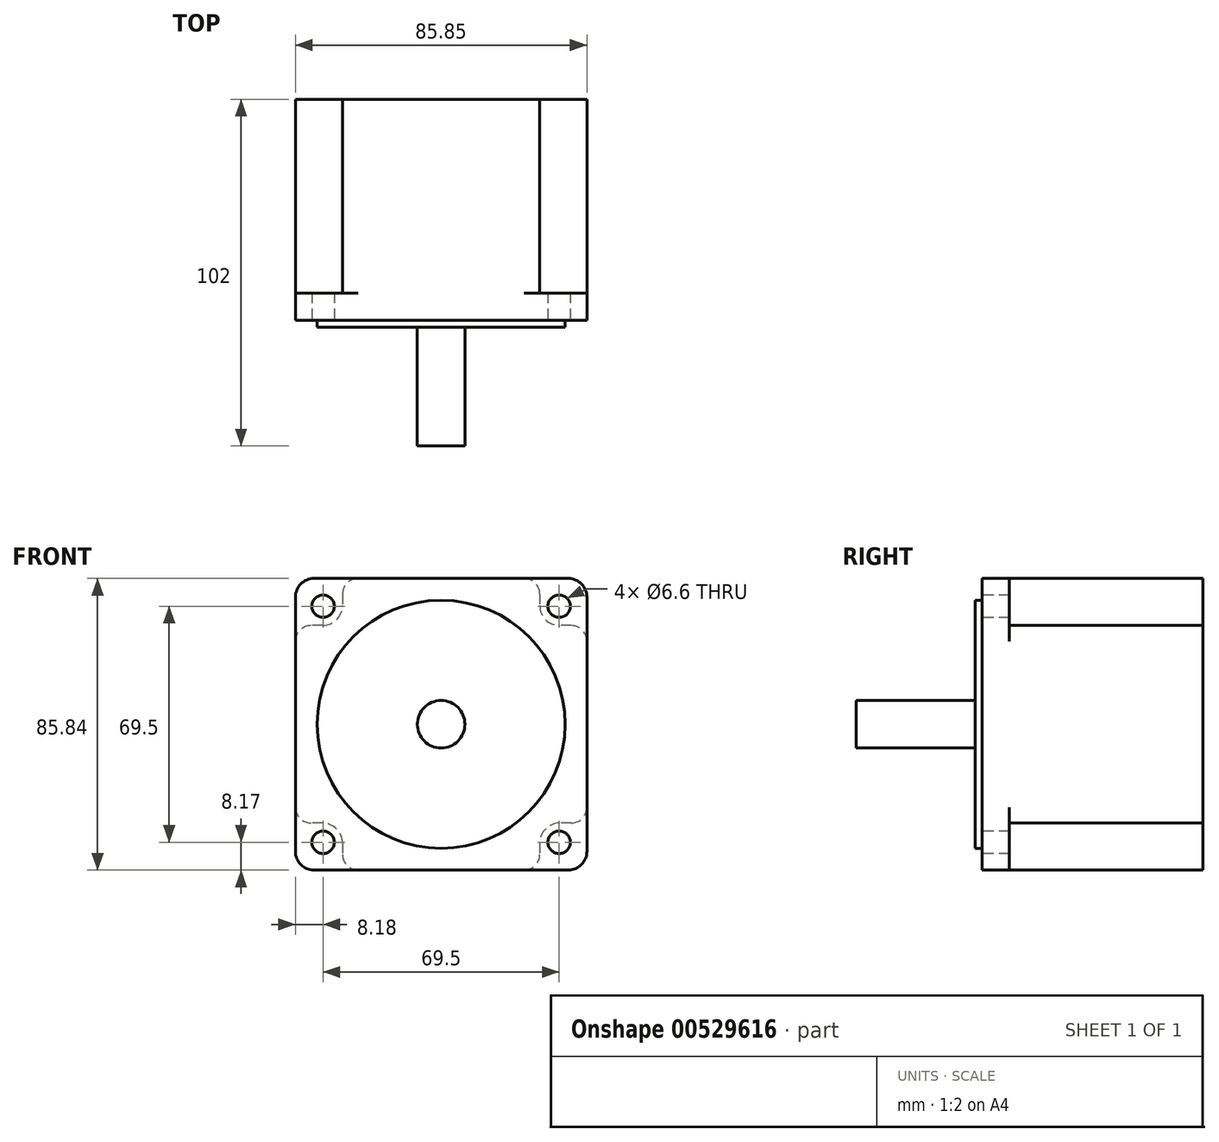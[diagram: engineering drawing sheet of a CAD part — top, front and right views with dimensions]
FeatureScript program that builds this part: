
annotation { "Feature Type Name" : "Feature", "Feature Type Description" : "" }
export const myFeature = defineFeature(function(context is Context, id is Id, definition is map)
    precondition{}
    {
        {
            var Q0;
            Q0=qCreatedBy(makeId("Front.planeOp"),FACE);
            var sketch = newSketch(context, id + "F0", { "sketchPlane" : qUnion([Q0])});
            skLineSegment(sketch, "E0.bottom", {"start": v(37.42, 42.93) * mm, "end": v(-37.43, 42.93) * mm});
            skLineSegment(sketch, "E0.top", {"start": v(37.42, -42.93) * mm, "end": v(-37.43, -42.93) * mm});
            skLineSegment(sketch, "E0.left", {"start": v(42.92, 37.43) * mm, "end": v(42.92, -37.43) * mm});
            skLineSegment(sketch, "E0.right", {"start": v(-42.93, 37.43) * mm, "end": v(-42.93, -37.43) * mm});
            skPoint(sketch, "E0.middle", {"position": v(0, 0) * mm});
            skPoint(sketch, "E1.visualSharp", {"position": v(-42.93, -42.93) * mm});
            skArc(sketch, "E1.filletArc", {"start": v(-42.93, -37.43) * mm, "mid": v(-41.31, -41.31) * mm, "end": v(-37.43, -42.93) * mm});
            skPoint(sketch, "E2.visualSharp", {"position": v(42.93, -42.93) * mm});
            skArc(sketch, "E2.filletArc", {"start": v(37.42, -42.93) * mm, "mid": v(41.31, -41.31) * mm, "end": v(42.92, -37.43) * mm});
            skPoint(sketch, "E3.visualSharp", {"position": v(42.92, 42.93) * mm});
            skArc(sketch, "E3.filletArc", {"start": v(42.92, 37.43) * mm, "mid": v(41.31, 41.31) * mm, "end": v(37.42, 42.93) * mm});
            skPoint(sketch, "E4.visualSharp", {"position": v(-42.93, 42.93) * mm});
            skArc(sketch, "E4.filletArc", {"start": v(-37.43, 42.93) * mm, "mid": v(-41.31, 41.31) * mm, "end": v(-42.93, 37.43) * mm});
            skCircle(sketch, "E5", {"center": v(-34.75, 34.75) * mm, "radius": 3.3 * mm});
            skCircle(sketch, "E6.MirrorC", {"center": v(34.75, 34.75) * mm, "radius": 3.3 * mm});
            skCircle(sketch, "E7.MirrorC", {"center": v(-34.75, -34.75) * mm, "radius": 3.3 * mm});
            skCircle(sketch, "E8.MirrorC", {"center": v(34.75, -34.75) * mm, "radius": 3.3 * mm});
            skLineSegment(sketch, "E9", {"start": v(-34.75, 34.75) * mm, "end": v(34.75, 34.75) * mm, "construction": true});
            skLineSegment(sketch, "E10", {"start": v(34.75, -34.75) * mm, "end": v(34.75, 34.75) * mm, "construction": true});
            skLineSegment(sketch, "E11", {"start": v(34.75, -34.75) * mm, "end": v(-34.75, -34.75) * mm, "construction": true});
            skLineSegment(sketch, "E12", {"start": v(-34.75, -34.75) * mm, "end": v(-34.75, 34.75) * mm, "construction": true});
            skCircle(sketch, "E13", {"center": v(0, 0) * mm, "radius": 36.51 * mm});
            skCircle(sketch, "E14", {"center": v(0, 0) * mm, "radius": 7 * mm});
            skSolve(sketch);
        }
        {
            var Q0;
            Q0=qCreatedBy(makeId("Front.planeOp"),FACE);
            var sketch = newSketch(context, id + "F1", { "sketchPlane" : qUnion([Q0])});
            skLineSegment(sketch, "E15.bottom", {"start": v(24.45, 42.93) * mm, "end": v(-24.45, 42.93) * mm});
            skLineSegment(sketch, "E15.top", {"start": v(24.45, -42.93) * mm, "end": v(-24.45, -42.93) * mm});
            skLineSegment(sketch, "E15.left", {"start": v(29.05, 38.33) * mm, "end": v(29.05, 34.95) * mm});
            skLineSegment(sketch, "E15.right", {"start": v(-29.05, 38.33) * mm, "end": v(-29.05, 34.95) * mm});
            skPoint(sketch, "E15.middle", {"position": v(0, 0) * mm});
            skLineSegment(sketch, "E16.bottom", {"start": v(38.32, 29.05) * mm, "end": v(34.95, 29.05) * mm});
            skLineSegment(sketch, "E16.top", {"start": v(38.32, -29.05) * mm, "end": v(34.95, -29.05) * mm});
            skLineSegment(sketch, "E16.left", {"start": v(42.92, 24.45) * mm, "end": v(42.92, -24.45) * mm});
            skLineSegment(sketch, "E16.right", {"start": v(-42.92, 24.45) * mm, "end": v(-42.92, -24.45) * mm});
            skPoint(sketch, "E17.visualSharp", {"position": v(-42.92, 29.05) * mm});
            skArc(sketch, "E17.filletArc", {"start": v(-38.32, 29.05) * mm, "mid": v(-41.58, 27.7) * mm, "end": v(-42.92, 24.45) * mm});
            skPoint(sketch, "E18.visualSharp", {"position": v(-42.92, -29.05) * mm});
            skArc(sketch, "E18.filletArc", {"start": v(-42.92, -24.45) * mm, "mid": v(-41.58, -27.7) * mm, "end": v(-38.32, -29.05) * mm});
            skPoint(sketch, "E19.visualSharp", {"position": v(-29.05, -42.93) * mm});
            skArc(sketch, "E19.filletArc", {"start": v(-29.05, -38.33) * mm, "mid": v(-27.7, -41.58) * mm, "end": v(-24.45, -42.93) * mm});
            skPoint(sketch, "E20.visualSharp", {"position": v(29.05, -42.93) * mm});
            skArc(sketch, "E20.filletArc", {"start": v(24.45, -42.93) * mm, "mid": v(27.7, -41.58) * mm, "end": v(29.05, -38.33) * mm});
            skPoint(sketch, "E21.visualSharp", {"position": v(42.92, -29.05) * mm});
            skArc(sketch, "E21.filletArc", {"start": v(38.32, -29.05) * mm, "mid": v(41.58, -27.7) * mm, "end": v(42.92, -24.45) * mm});
            skPoint(sketch, "E22.visualSharp", {"position": v(42.92, 29.05) * mm});
            skArc(sketch, "E22.filletArc", {"start": v(42.92, 24.45) * mm, "mid": v(41.58, 27.7) * mm, "end": v(38.32, 29.05) * mm});
            skPoint(sketch, "E23.visualSharp", {"position": v(29.05, 42.93) * mm});
            skArc(sketch, "E23.filletArc", {"start": v(29.05, 38.33) * mm, "mid": v(27.7, 41.58) * mm, "end": v(24.45, 42.92) * mm});
            skPoint(sketch, "E24.visualSharp", {"position": v(-29.05, 42.93) * mm});
            skArc(sketch, "E24.filletArc", {"start": v(-24.45, 42.92) * mm, "mid": v(-27.7, 41.58) * mm, "end": v(-29.05, 38.33) * mm});
            skLineSegment(sketch, "E25.trimOffspring", {"start": v(-34.95, 29.05) * mm, "end": v(-38.32, 29.05) * mm});
            skLineSegment(sketch, "E26.trimOffspring", {"start": v(-29.05, -34.95) * mm, "end": v(-29.05, -38.33) * mm});
            skLineSegment(sketch, "E27.trimOffspring", {"start": v(-34.95, -29.05) * mm, "end": v(-38.32, -29.05) * mm});
            skLineSegment(sketch, "E28.trimOffspring", {"start": v(29.05, -34.95) * mm, "end": v(29.05, -38.33) * mm});
            skPoint(sketch, "E29.visualSharp", {"position": v(-29.05, 29.05) * mm});
            skArc(sketch, "E29.filletArc", {"start": v(-34.95, 29.05) * mm, "mid": v(-30.78, 30.78) * mm, "end": v(-29.05, 34.95) * mm});
            skPoint(sketch, "E30.visualSharp", {"position": v(29.05, 29.05) * mm});
            skArc(sketch, "E30.filletArc", {"start": v(29.05, 34.95) * mm, "mid": v(30.78, 30.78) * mm, "end": v(34.95, 29.05) * mm});
            skPoint(sketch, "E31.visualSharp", {"position": v(29.05, -29.05) * mm});
            skArc(sketch, "E31.filletArc", {"start": v(34.95, -29.05) * mm, "mid": v(30.78, -30.78) * mm, "end": v(29.05, -34.95) * mm});
            skPoint(sketch, "E32.visualSharp", {"position": v(-29.05, -29.05) * mm});
            skArc(sketch, "E32.filletArc", {"start": v(-29.05, -34.95) * mm, "mid": v(-30.78, -30.78) * mm, "end": v(-34.95, -29.05) * mm});
            skSolve(sketch);
        }
        {
            var Q0;
            Q0=makeQuery(id+"F0.imprint","IMPRINT",FACE,{"disambiguationData":[TD([[makeQuery(id+"F0.imprint","IMPRINT",EDGE,{"derivedFrom":sQuery(id+"F0.wireOp",EDGE,"E13")}),1.0]])]});
            extrude(context, id + "F2", {"entities" : qUnion([Q0]), "depth" : 2 * mm, "offsetDistance" : 25 * mm});
        }
        {
            var Q0;
            Q0=makeQuery(id+"F0.imprint","IMPRINT",FACE,{"disambiguationData":[TD([[makeQuery(id+"F0.imprint","IMPRINT",EDGE,{"derivedFrom":sQuery(id+"F0.wireOp",EDGE,"E14")}),1.0]])]});
            extrude(context, id + "F3", {"entities" : qUnion([Q0]), "operationType" : NewBodyOperationType.ADD, "depth" : 37 * mm, "offsetDistance" : 25 * mm});
        }
        {
            var Q0;
            Q0=makeQuery(id+"F0.imprint","IMPRINT",FACE,{"disambiguationData":[TD([[makeQuery(id+"F0.imprint","IMPRINT",EDGE,{"derivedFrom":sQuery(id+"F0.wireOp",EDGE,"E0.bottom")}),1.0]])]});
            var Q1;
            Q1=makeQuery(id+"F0.imprint","IMPRINT",FACE,{"disambiguationData":[TD([[makeQuery(id+"F0.imprint","IMPRINT",EDGE,{"derivedFrom":sQuery(id+"F0.wireOp",EDGE,"E13")}),1.0]])]});
            extrude(context, id + "F4", {"entities" : qUnion([Q0, Q1]), "oppositeDirection" : true, "depth" : 8 * mm, "offsetDistance" : 25 * mm});
        }
        {
            var Q0;
            Q0 = qSketchRegion(id + "F1", true);
            extrude(context, id + "F5", {"entities" : qUnion([Q0]), "operationType" : NewBodyOperationType.ADD, "oppositeDirection" : true, "depth" : 65 * mm, "offsetDistance" : 25 * mm});
        }
    });
